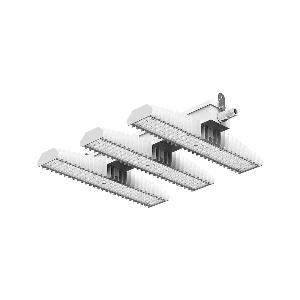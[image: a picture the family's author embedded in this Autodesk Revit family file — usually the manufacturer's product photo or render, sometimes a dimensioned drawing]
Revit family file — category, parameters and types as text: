
# Revit family: 3f_filippi_-_3f_lem_medio_3f_filippi_-_58912_-_3f_lem_3_led_150_dali_cr_medio
name_source: partatom
category: Lighting Fixtures
units: mm (PartAtom-declared; Revit-internal decimal feet)

## family parameters
Cut with Voids When Loaded = No
Host = Face
Light Source = No
Part Type = Normal
Room Calculation Point = No
Round Connector Dimension = Use Diameter
Shared = No

## types (1)
- 3F Filippi - 3F LEM Medio (1 x LED, 24944 lm, 165 W, 4000 K)
    Apparent Load = 165 VA
    Approval mark = CE
    CIE Flux Codes = 83 96 99 100 100
    Color Rendering = 80
    Color Temperature = 4000 K
    Control Gear = Electronic transformer
    Default Elevation = 1800 mm
    Description = Industrial luminaire with high light output and high luminous efficiency designed with the most innovative technologies for environments with temperature up to 55°C.

ILLUMINOTECHNICAL
Luminous efficiency 100% (DLOR 100%, ULOR 0%).
Initial luminous flux of the luminaire 24944 lm.
Medium distribution with rectangular shape.
Installation Interdistance Transv.D = 1.02 x hu - Long.D = 1.06 x hu.
Tabular UGR (CIE 117 - 4H-8H; S=0.25H; 70/50/20): RUG 19.2 - 18.8.
Beam angle: 65° - 67°.
Luminous efficacy 151 lm/W.
Lifetime (L93/B10): 30000 h. (tq+25°C)
Lifetime (L90/B10): 50000 h. (tq+25°C)
Lifetime (L85/B10): 80000 h. (tq+25°C)
Lifetime (L80/B10): 100000 h. (tq+25°C)
Lifetime (L85/B10): 50000 h. (tq+55°C)
Sudden decreased luminous flux after 50000 hours: 0% (C0).
Photobiological safety in compliance with IEC/TR 62778: RG0 risk exempt, (IEC 62471).
In compliance with IEC/EN 62722-2-1 - IEC/EN 62717 standards.

SOURCE
3 Mid-Power linear LED modules 50W/840.
Energy efficiency class (UE 2019/2020 - UE 2019/2015): C.
CIE 13.3 Colour rendering index: CRI >80 (R9 <50%).
IES TM-30 Fidelity Index: Rf = 84 Rg = 95.
CCT nominal colour temperature 4000 K.
Colour initial tolerance (MacAdam): SDCM 3.

MECHANICAL
Passive modular heatsinks in die-casted aluminium, painted in white colour.
To optimize the thermal management of the LED module, the heatsinks are oversized and provided with self-cleaning of cooling fins.
Wiring body in aluminium and galvanised steel anchored solidly to the sinks and thermally separated.
3F Lens lenses with high luminous efficiency, transparent methacrylate (PMMA), fixed to the LED modules.
Fixing brackets in stainless steel.
Luminaire with limited surface temperature. - D - (EN 60598-2-24)
Dimensions: 657x542 mm, height 129 mm. Weight 14 kg.
IP65 protection degree.
Mechanical strength to impacts IK06 (1 joule).
Glow-wire test resistance 650°C.

ELECTRICAL
Halogen Free DALI-2 DATI (Parts 251, 252, 253), PUSH-DIM, electronic wiring 230V-50/60Hz, power factor 0.97 at full load, THD <25%, constant output current, class I, 2 driver, 2 DALI addresses.
Power of the luminaire 165 W.
ENEC - CE.
SAFE FLICKER: PstLM=<1 and SVM=<0.4 (IEC TR 61547-1 and IEC TR 63158), to ensure a more comfortable and safe light.
Luminaire compliant with EN 60598-2-22 for power supply from a centralised emergency system CPSS (Central Power Supply System), not incorporated in the luminaire - high risk areas excluded. The default power and flux are 100% in AC and 15% in DC.
Ambient temperature from -30°C to +55°C.
Temperature class T6 max 85°C.
Quick connection via M25 5P connector with 9-13 mm tightening range.
Power unit positioned on a separate compartment by the LED module to ensure optimum temperatures of cabling components, to be inspectable and maintainable.
Relative humidity UR: <85%.

INSTALLATION
Ceiling / Suspended / Wall.
All accessories dedicated to this product are available on the Catalog and on our website www.3F-Filippi.com.

APPLICATIONS
In commercial environments, exhibition and industrial areas, stores, open areas.
Applications with high ambient temperature up to 55°C.
Environments in which it is necessary a total protection against falling fragments (eg environments with foodstuffs or machines with moving parts or with extreme temperature changes), use luminaires with polycarbonate lenses.

LIGHT MANAGEMENT
Recommended minimum setting: 10%.
The luminaire, equipped with (DALI-2 DATI) driver, can be controlled manually with 3F Easy Dim technology or automatically/manually with wired or wireless DALI/D2D control systems.
The D2D driver guarantees interoperability with other devices with the same certification by making the following information available:
Device Data (Part 251), Energy Report (Part 252), Diagnosis & Maintenance (Part 253).
In electrical systems without a regulation system (manual or automatic) and DALI bus, a suitable jumper must be made on the DA-DA terminals of the appliance.

WARNING
Fixture not suitable for cold stores with an ambient temperature <0°C and/or relative humidity >85%.
Luminaire designed for disposal/recycling at end-of-life.
Replaceable (LED only) light source by a professional. Replaceable control gear by a professional.
    Height = 129 mm
    Lamp = 1 x LED
    Lamp Light Flux = 24944 lm
    Lamp Power = 165 W
    Lamp count = 1
    Length = 657 mm
    Lifetime = 50000 h
    Luminous efficacy = 151 lm/W
    Manufacturer = 3F Filippi
    ModVariant = No
    Model = 3F Filippi - 58912 - 3F LEM 3 LED 150 DALI CR MEDIO
    Mounting Place = Ceiling
    Mounting Type = Pendant
    Number of Poles = 1
    OnlyDefault = Yes
    Power Factor = 1
    Product Name = 3F Filippi - 3F LEM Medio
    Product group = pendant luminaire
    ProductGroupID = 9
    Protection Class = Protection class I
    Protection Degree = IP 65
    RLX_Detail_Level = 1
    RLX_Emergency_Light_Flux = 0 lm
    RLX_Emergency_Type = 0
    RLX_Emergency_Type_DB = No
    RlxData = <blob elided: 103013 chars, md5=219d63db>
    Socket = socket
    Standby Power = 0 W
    System Light Flux = 24944 lm
    System Power = 165 W
    Type Comments = Product without accessories
    Type Image = 3f_filippi_-_lem_3.jpg
    URL = http://relux.com
    VarID = ---
    Voltage = 0 V
    Weight = 0.00 kg
    Width = 542 mm

## geometry (parser evidence)
native form markers: Blend x4, Sweep x10
no freeform markers — native parametric forms only
